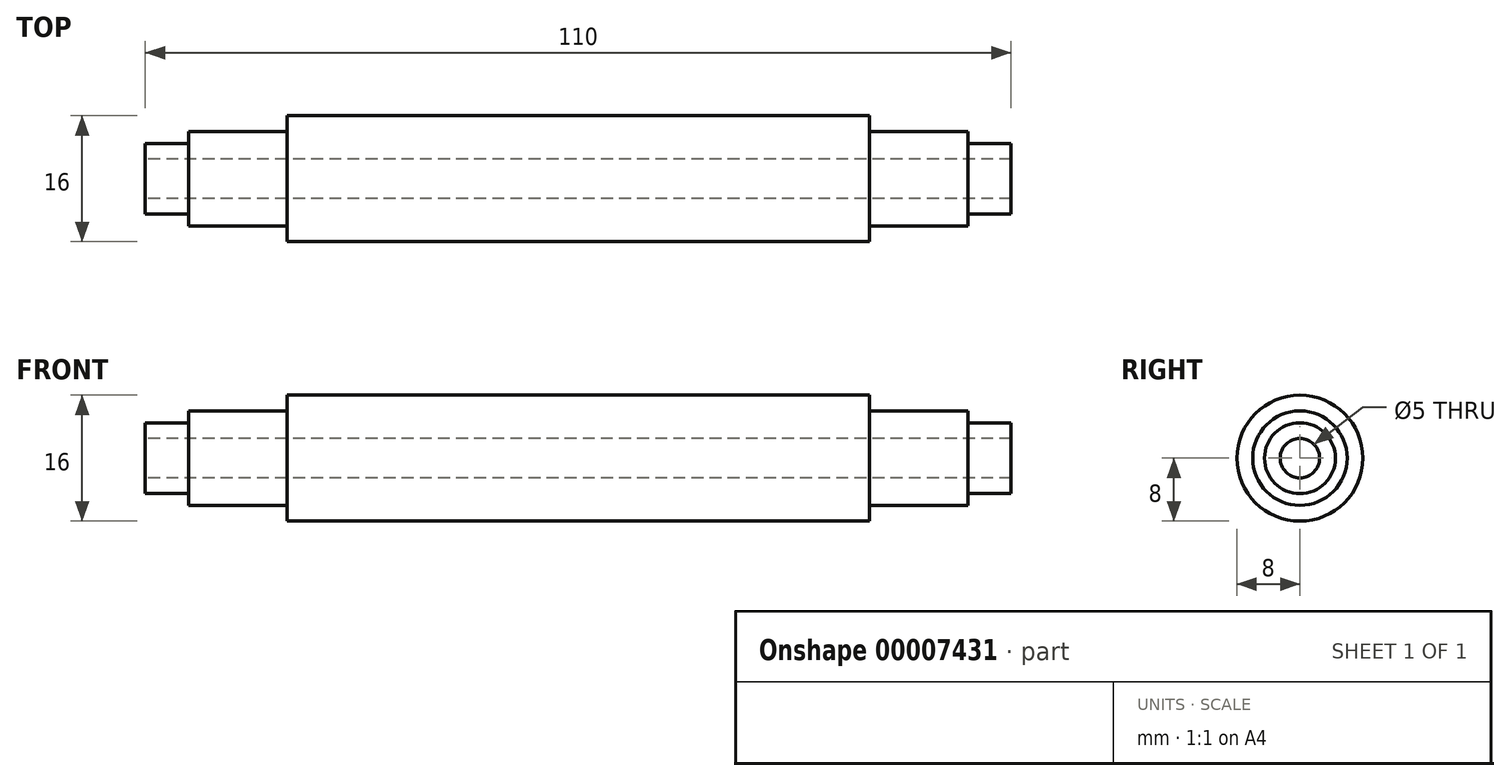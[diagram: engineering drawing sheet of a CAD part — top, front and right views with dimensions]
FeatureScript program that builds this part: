
annotation { "Feature Type Name" : "Feature", "Feature Type Description" : "" }
export const myFeature = defineFeature(function(context is Context, id is Id, definition is map)
    precondition{}
    {
        {
            var Q0;
            Q0=qCreatedBy(makeId("Top.planeOp"),FACE);
            var sketch = newSketch(context, id + "F0", { "sketchPlane" : qUnion([Q0])});
            skLineSegment(sketch, "E0", {"start": v(55, 0) * mm, "end": v(-55, 0) * mm});
            skLineSegment(sketch, "E1", {"start": v(-55, 0) * mm, "end": v(-55, -2) * mm});
            skLineSegment(sketch, "E2", {"start": v(-55, -2) * mm, "end": v(-49.5, -2) * mm});
            skLineSegment(sketch, "E3", {"start": v(-49.5, -2) * mm, "end": v(-49.5, -3.5) * mm});
            skLineSegment(sketch, "E4", {"start": v(-49.5, -3.5) * mm, "end": v(-37, -3.5) * mm});
            skLineSegment(sketch, "E5", {"start": v(-37, -3.5) * mm, "end": v(-37, -5.5) * mm});
            skLineSegment(sketch, "E6", {"start": v(-37, -5.5) * mm, "end": v(0, -5.5) * mm});
            skLineSegment(sketch, "E7", {"start": v(0, -5.5) * mm, "end": v(37, -5.5) * mm});
            skLineSegment(sketch, "E8", {"start": v(37, -5.5) * mm, "end": v(37, -3.5) * mm});
            skLineSegment(sketch, "E9", {"start": v(37, -3.5) * mm, "end": v(49.5, -3.5) * mm});
            skLineSegment(sketch, "E10", {"start": v(49.5, -3.5) * mm, "end": v(49.5, -2) * mm});
            skLineSegment(sketch, "E11", {"start": v(49.5, -2) * mm, "end": v(55, -2) * mm});
            skLineSegment(sketch, "E12", {"start": v(55, -2) * mm, "end": v(55, 0) * mm});
            skLineSegment(sketch, "E13", {"start": v(-55, 2.5) * mm, "end": v(55, 2.5) * mm});
            skSolve(sketch);
        }
        {
            var Q0;
            Q0=makeQuery(id+"F0.imprint","IMPRINT",FACE,{"disambiguationData":[TD([[makeQuery(id+"F0.imprint","IMPRINT",EDGE,{"derivedFrom":sQuery(id+"F0.wireOp",EDGE,"E0")}),1.0]])]});
            var Q1;
            Q1=sQuery(id+"F0.wireOp",EDGE,"E13");
            revolve(context, id + "F1", {"entities" : qUnion([Q0]), "axis" : qUnion([Q1]), "revolveType" : RevolveType.FULL});
        }
        {
            var Q0;
            Q0=makeQuery(id+"F0.imprint","IMPRINT",FACE,{"disambiguationData":[TD([[makeQuery(id+"F0.imprint","IMPRINT",EDGE,{"derivedFrom":sQuery(id+"F0.wireOp",EDGE,"E0")}),1.0]])]});
            var Q1;
            Q1=sQuery(id+"F0.wireOp",EDGE,"E13");
            revolve(context, id + "F2", {"entities" : qUnion([Q0]), "axis" : qUnion([Q1]), "revolveType" : RevolveType.FULL});
        }
        {
            var Q0;
            Q0=makeQuery(id+"F1.opRevolve","SWEPT_BODY",BODY,{"disambiguationData":[OSD([sQuery(id+"F0.wireOp",EDGE,"E0"),sQuery(id+"F0.wireOp",EDGE,"E1"),sQuery(id+"F0.wireOp",EDGE,"E2"),sQuery(id+"F0.wireOp",EDGE,"E3"),sQuery(id+"F0.wireOp",EDGE,"E4"),sQuery(id+"F0.wireOp",EDGE,"E5"),sQuery(id+"F0.wireOp",EDGE,"E6"),sQuery(id+"F0.wireOp",EDGE,"E7"),sQuery(id+"F0.wireOp",EDGE,"E8"),sQuery(id+"F0.wireOp",EDGE,"E9"),sQuery(id+"F0.wireOp",EDGE,"E10"),sQuery(id+"F0.wireOp",EDGE,"E11"),sQuery(id+"F0.wireOp",EDGE,"E12")])]});
            deleteBodies(context, id + "F3", {"entities" : qUnion([Q0])});
        }
    });
